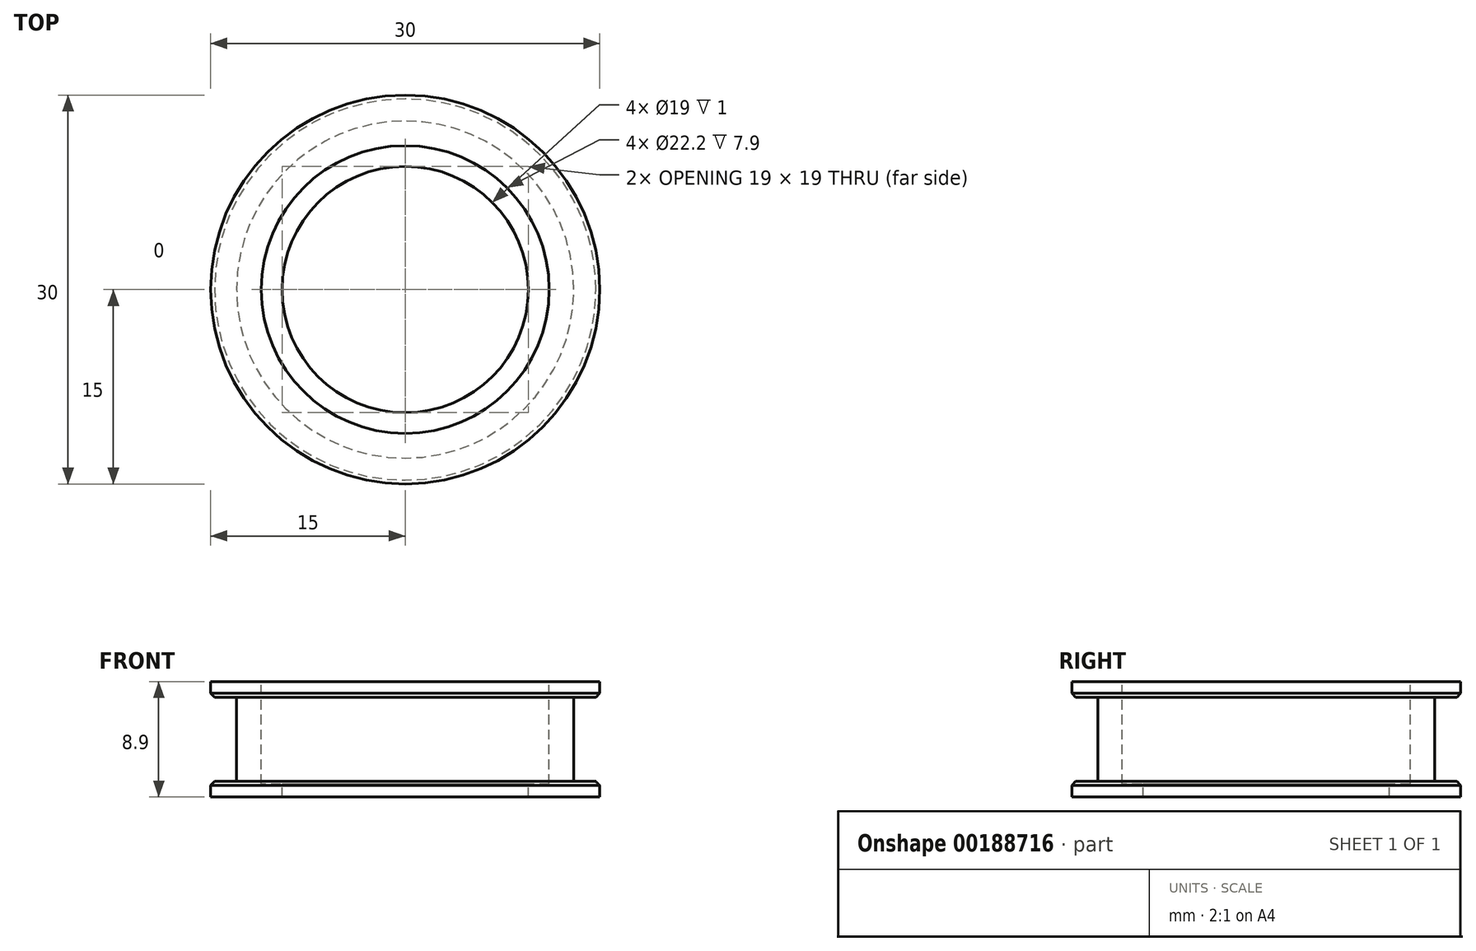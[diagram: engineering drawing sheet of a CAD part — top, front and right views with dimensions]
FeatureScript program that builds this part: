
annotation { "Feature Type Name" : "Feature", "Feature Type Description" : "" }
export const myFeature = defineFeature(function(context is Context, id is Id, definition is map)
    precondition{}
    {
        {
            var Q0;
            Q0=qCreatedBy(makeId("Front.planeOp"),FACE);
            var sketch = newSketch(context, id + "F0", { "sketchPlane" : qUnion([Q0])});
            skLineSegment(sketch, "E0", {"start": v(0, 4.45) * mm, "end": v(15, 4.45) * mm});
            skLineSegment(sketch, "E1", {"start": v(15, 4.45) * mm, "end": v(15, 3.25) * mm});
            skLineSegment(sketch, "E2", {"start": v(15, 3.25) * mm, "end": v(13, 3.25) * mm});
            skLineSegment(sketch, "E3", {"start": v(13, 3.25) * mm, "end": v(13, -3.25) * mm});
            skLineSegment(sketch, "E4", {"start": v(13, -3.25) * mm, "end": v(15, -3.25) * mm});
            skLineSegment(sketch, "E5", {"start": v(15, -3.25) * mm, "end": v(15, -4.45) * mm});
            skLineSegment(sketch, "E6", {"start": v(15, -4.45) * mm, "end": v(0, -4.45) * mm});
            skPoint(sketch, "E7", {"position": v(0, 0) * mm});
            skLineSegment(sketch, "E8", {"start": v(0, 4.45) * mm, "end": v(0, -4.45) * mm});
            skSolve(sketch);
        }
        {
            var Q0;
            Q0=makeQuery(id+"F0.imprint","IMPRINT",FACE,{"disambiguationData":[TD([[makeQuery(id+"F0.imprint","IMPRINT",EDGE,{"derivedFrom":sQuery(id+"F0.wireOp",EDGE,"E0")}),-1.0]])]});
            var Q1;
            Q1=sQuery(id+"F0.wireOp",EDGE,"E0");
            var Q2;
            Q2=sQuery(id+"F0.wireOp",EDGE,"E1");
            var Q3;
            Q3=sQuery(id+"F0.wireOp",EDGE,"E6");
            var Q4;
            Q4=sQuery(id+"F0.wireOp",EDGE,"E2");
            var Q5;
            Q5=sQuery(id+"F0.wireOp",EDGE,"E4");
            var Q6;
            Q6=sQuery(id+"F0.wireOp",EDGE,"E5");
            var Q7;
            Q7=sQuery(id+"F0.wireOp",EDGE,"E3");
            var Q8;
            Q8=sQuery(id+"F0.wireOp",EDGE,"E8");
            revolve(context, id + "F1", {"entities" : qUnion([Q0]), "surfaceEntities" : qUnion([Q1, Q2, Q3, Q4, Q5, Q6, Q7]), "axis" : qUnion([Q8]), "revolveType" : RevolveType.FULL});
        }
        {
            var Q0;
            Q0=makeQuery(id+"F1.opRevolve","SWEPT_FACE",FACE,{"disambiguationData":[OSD([sQuery(id+"F0.wireOp",EDGE,"E0")])]});
            var sketch = newSketch(context, id + "F2", { "sketchPlane" : qUnion([Q0])});
            skCircle(sketch, "E9", {"center": v(0, 0) * mm, "radius": 9.5 * mm});
            skCircle(sketch, "E10", {"center": v(0, 0) * mm, "radius": 11.1 * mm});
            skSolve(sketch);
        }
        {
            var Q0;
            Q0=makeQuery(id+"F2.imprint","IMPRINT",FACE,{"disambiguationData":[TD([[makeQuery(id+"F2.imprint","IMPRINT",EDGE,{"derivedFrom":sQuery(id+"F2.wireOp",EDGE,"E9")}),1.0]])]});
            extrude(context, id + "F3", {"entities" : qUnion([Q0]), "operationType" : NewBodyOperationType.REMOVE, "endBound" : BoundingType.UP_TO_NEXT, "oppositeDirection" : true, "depth" : 25 * mm});
        }
        {
            var Q0;
            Q0=makeQuery(id+"F2.imprint","IMPRINT",FACE,{"disambiguationData":[TD([[makeQuery(id+"F2.imprint","IMPRINT",EDGE,{"derivedFrom":sQuery(id+"F2.wireOp",EDGE,"E9")}),-1.0]])]});
            extrude(context, id + "F4", {"entities" : qUnion([Q0]), "operationType" : NewBodyOperationType.REMOVE, "oppositeDirection" : true, "depth" : 7.9 * mm});
        }
        {
            var Q0;
            Q0=makeQuery(id+"F1.opRevolve","SWEPT_EDGE",EDGE,{"disambiguationData":[OSD([sQuery(id+"F0.wireOp",EDGE,"E4"),sQuery(id+"F0.wireOp",EDGE,"E5")])]});
            var Q1;
            Q1=makeQuery(id+"F1.opRevolve","SWEPT_EDGE",EDGE,{"disambiguationData":[OSD([sQuery(id+"F0.wireOp",EDGE,"E1"),sQuery(id+"F0.wireOp",EDGE,"E2")])]});
            chamfer(context, id + "F5", {"entities" : qUnion([Q0, Q1]), "width" : .3 * mm, "tangentPropagation" : true});
        }
    });
